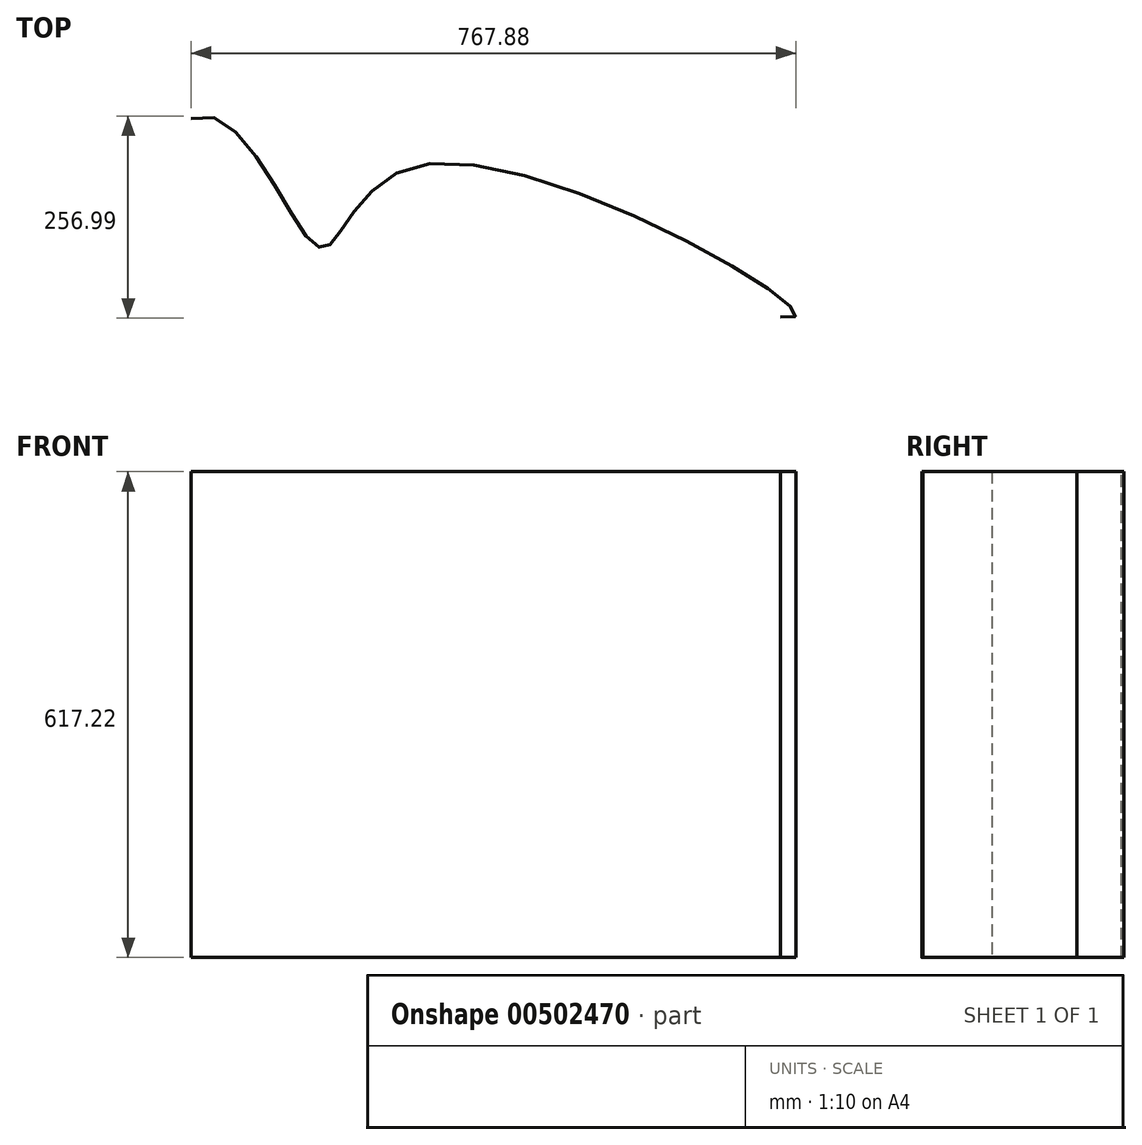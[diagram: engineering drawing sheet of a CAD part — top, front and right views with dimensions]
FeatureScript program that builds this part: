
annotation { "Feature Type Name" : "Feature", "Feature Type Description" : "" }
export const myFeature = defineFeature(function(context is Context, id is Id, definition is map)
    precondition{}
    {
        {
            var Q0;
            Q0=qCreatedBy(makeId("Top.planeOp"),FACE);
            var sketch = newSketch(context, id + "F0", { "sketchPlane" : qUnion([Q0])});
            skFitSpline(sketch, "E0", {"points": [v(431.77, 116.4) * mm, v(-17.74, 310.93) * mm, v(-156.1, 205.85) * mm, v(-316.71, 368.84) * mm], "startDerivative": vector(763.12, -141.08) * mm, "endDerivative": vector(-683.56, -291.95) * mm});
            skLineSegment(sketch, "E1", {"start": v(-316.71, 368.84) * mm, "end": v(431.77, 116.4) * mm});
            skSolve(sketch);
        }
        {
            var Q0;
            Q0=sQuery(id+"F0.wireOp",EDGE,"E0");
            extrude(context, id + "F1", {"bodyType" : ToolBodyType.SURFACE, "surfaceEntities" : qUnion([Q0]), "depth" : 617.22 * mm, "offsetDistance" : 25.4 * mm});
        }
    });
